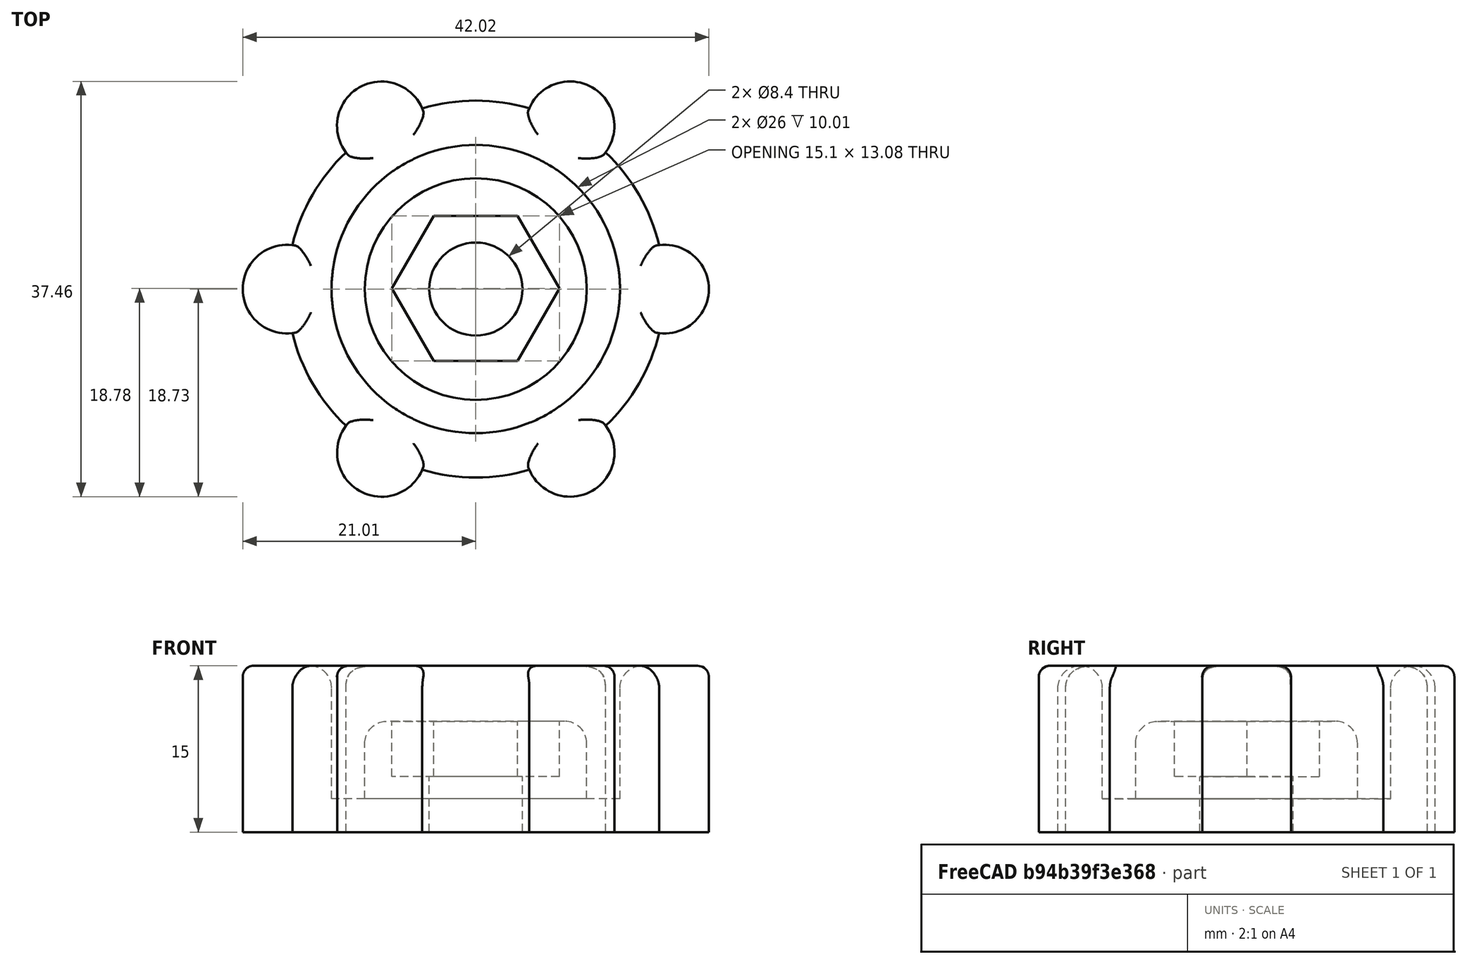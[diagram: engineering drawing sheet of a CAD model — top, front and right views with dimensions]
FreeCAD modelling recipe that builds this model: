
FCSTD DOCUMENT  (FreeCAD 0.15R4630 (Git))
Label: manual_control
License: All rights reserved
LicenseURL: http://en.wikipedia.org/wiki/All_rights_reserved
objects: Part::Feature×7, Part::Cylinder×6, Part::Fillet×4, Part::MultiFuse×3, Part::Cut×3, Mesh::Feature×1, Part::Prism×1
note: 24 computed .brp shape members not serialized (recipe doc carries the construction recipe); baked Part::Feature solids carry a one-line shape summary decoded from their .brp

FEATURE [Mesh::Feature] Manualcontrol
FEATURE [Part::Feature] Manualcontrol001001  label="Manualcontrol002"
  shape: bbox 42 x 37.45 x 15 mm, 21926 faces, 0 solids (baked)
FEATURE [Part::Cylinder] Cylinder  label="Cilindro"
  Angle = 360
  Height = 15
  Placement = pos=(21,18.73,0) rot=(0,0,1;0rad)
  Radius = 17
FEATURE [Part::Cylinder] Cylinder001  label="Cilindro001"
  Angle = 360
  Height = 15
  Placement = pos=(12.5,4,0) rot=(0,0,1;0rad)
  Radius = 4
FEATURE [Part::Fillet] Fillet
  Base = -> Cylinder001
  Edges = 1 edges r=1: [Edge1]
FEATURE [Part::Feature] Fillet001
  Placement = pos=(-5.72066,27.5515,0) rot=(0,0,1;5.23599rad)
  shape: bbox 8.364 x 8.364 x 15 mm, 4 faces (baked)
FEATURE [Part::Feature] Fillet002
  Placement = pos=(26.7207,-8.82153,0) rot=(0,0,1;1.0472rad)
  shape: bbox 8.364 x 8.364 x 15 mm, 4 faces (baked)
FEATURE [Part::Feature] Fillet003
  Placement = pos=(47.7207,9.90847,0) rot=(0,0,1;2.0944rad)
  shape: bbox 8.364 x 8.364 x 15 mm, 4 faces (baked)
FEATURE [Part::Feature] Fillet004
  Placement = pos=(42,37.46,0) rot=(0,0,1;3.14159rad)
  shape: bbox 8.659 x 8.659 x 15 mm, 4 faces (baked)
FEATURE [Part::Feature] Fillet005
  Placement = pos=(15.2793,46.2815,0) rot=(0,0,1;4.18879rad)
  shape: bbox 8.364 x 8.364 x 15 mm, 4 faces (baked)
FEATURE [Part::MultiFuse] Fusion
  Shapes = -> [Fillet,Fillet002,Fillet005,Fillet003,Fillet004,Fillet001]
FEATURE [Part::Cylinder] Cylinder002  label="Cilindro002"
  Angle = 360
  Height = 15
  Placement = pos=(21,18.73,0) rot=(0,0,1;0rad)
  Radius = 13
FEATURE [Part::Cut] Cut
  Base = -> Cylinder
  Tool = -> Cylinder002
FEATURE [Part::Fillet] Fillet006
  Base = -> Cut
  Edges = 1 edges r=1.99: [Edge1]
FEATURE [Part::MultiFuse] Fusion001
  Shapes = -> [Fillet006,Fusion]
FEATURE [Part::Fillet] Fillet007
  Base = -> Fusion001
  Edges = 1 edges r=1.99: [Edge3]
FEATURE [Part::Cylinder] Cylinder003  label="Cilindro003"
  Angle = 360
  Height = 10
  Placement = pos=(21,18.73,0) rot=(0,0,1;0rad)
  Radius = 10
FEATURE [Part::Cylinder] Cylinder004  label="Cilindro004"
  Angle = 360
  Height = 3
  Placement = pos=(21,18.73,0) rot=(0,0,1;0rad)
  Radius = 14
FEATURE [Part::MultiFuse] Fusion002
  Shapes = -> [Cylinder003,Cylinder004,Fillet007]
FEATURE [Part::Cylinder] Cylinder005  label="Cilindro005"
  Angle = 360
  Height = 12
  Placement = pos=(21,18.73,-1) rot=(0,0,1;0rad)
  Radius = 4.2
FEATURE [Part::Cut] Cut001
  Base = -> Fusion002
  Tool = -> Cylinder005
FEATURE [Part::Fillet] Fillet008
  Base = -> Cut001
  Edges = 1 edges r=1.99: [Edge1]
FEATURE [Part::Prism] Prism  label="Prisma"
  Circumradius = 7.55
  Height = 5
  Placement = pos=(21,18.78,5) rot=(0,0,1;0rad)
  Polygon = 6
FEATURE [Part::Cut] Cut002  label="manual_control"
  Base = -> Fillet008
  Tool = -> Prism
FEATURE [Part::Feature] Cut003  label="manual_control001"
  shape: bbox 42.38 x 38.12 x 15 mm, 58 faces (baked)
